FCSTD DOCUMENT  (FreeCAD 0.20R0.20)
Label: 003
License: All rights reserved
LicenseURL: http://en.wikipedia.org/wiki/All_rights_reserved
objects: Sketcher::SketchObject×1
note: 1 computed .brp shape members not serialized (recipe doc carries the construction recipe); baked Part::Feature solids carry a one-line shape summary decoded from their .brp

FEATURE [Sketcher::SketchObject] Sketch
  FullyConstrained = true
  sketch-geometry (16):
    g0: LineSegment StartX=0 StartY=0 StartZ=0 EndX=0 EndY=200 EndZ=0
    g1: LineSegment StartX=390 StartY=200 StartZ=0 EndX=390 EndY=0 EndZ=0
    g2: LineSegment StartX=0 StartY=200 StartZ=0 EndX=190 EndY=200 EndZ=0
    g3: LineSegment StartX=0 StartY=0 StartZ=0 EndX=190 EndY=0 EndZ=0
    g4: LineSegment StartX=390 StartY=200 StartZ=0 EndX=200 EndY=200 EndZ=0
    g5: LineSegment StartX=390 StartY=0 StartZ=0 EndX=200 EndY=0 EndZ=0
    g6: LineSegment StartX=190 StartY=200 StartZ=0 EndX=190 EndY=186 EndZ=0
    g7: LineSegment StartX=190 StartY=0 StartZ=0 EndX=190 EndY=14 EndZ=0
    g8: LineSegment StartX=200 StartY=0 StartZ=0 EndX=200 EndY=14 EndZ=0
    g9: LineSegment StartX=200 StartY=200 StartZ=0 EndX=200 EndY=186 EndZ=0
    g10: LineSegment StartX=190 StartY=186 StartZ=0 EndX=16 EndY=186 EndZ=0
    g11: LineSegment StartX=190 StartY=14 StartZ=0 EndX=16 EndY=14 EndZ=0
    g12: LineSegment StartX=200 StartY=14 StartZ=0 EndX=374 EndY=14 EndZ=0
    g13: LineSegment StartX=200 StartY=186 StartZ=0 EndX=374 EndY=186 EndZ=0
    g14: LineSegment StartX=16 StartY=186 StartZ=0 EndX=16 EndY=14 EndZ=0
    g15: LineSegment StartX=374 StartY=186 StartZ=0 EndX=374 EndY=14 EndZ=0
  constraints (46):
    c: Coincident(g0,g-1)
    c: Vertical(g0)
    c: Distance(g0) = 200
    c: Vertical(g1)
    c: Distance(g1) = 200
    c: Coincident(g2,g0)
    c: Horizontal(g2)
    c: Distance(g2) = 190
    c: Coincident(g3,g0)
    c: Horizontal(g3)
    c: Distance(g3) = 190
    c: Block(g1)
    c: Coincident(g4,g1)
    c: Horizontal(g4)
    c: Coincident(g5,g1)
    c: Horizontal(g5)
    c: Distance(g5) = 190
    c: Distance(g4) = 190
    c: Coincident(g6,g2)
    c: Vertical(g6)
    c: Distance(g6) = 14
    c: Coincident(g7,g3)
    c: Vertical(g7)
    c: Coincident(g8,g5)
    c: Vertical(g8)
    c: Coincident(g9,g4)
    c: Vertical(g9)
    c: Distance(g9) = 14
    c: Distance(g7) = 14
    c: Distance(g8) = 14
    c: Coincident(g10,g6)
    c: Horizontal(g10)
    c: Coincident(g11,g7)
    c: Horizontal(g11)
    c: Coincident(g12,g8)
    c: Horizontal(g12)
    c: Coincident(g13,g9)
    c: Horizontal(g13)
    c: Distance(g13) = 174
    c: Distance(g12) = 174
    c: Distance(g11) = 174
    c: Distance(g10) = 174
    c: Coincident(g14,g10)
    c: Coincident(g14,g11)
    c: Coincident(g15,g13)
    c: Coincident(g15,g12)
